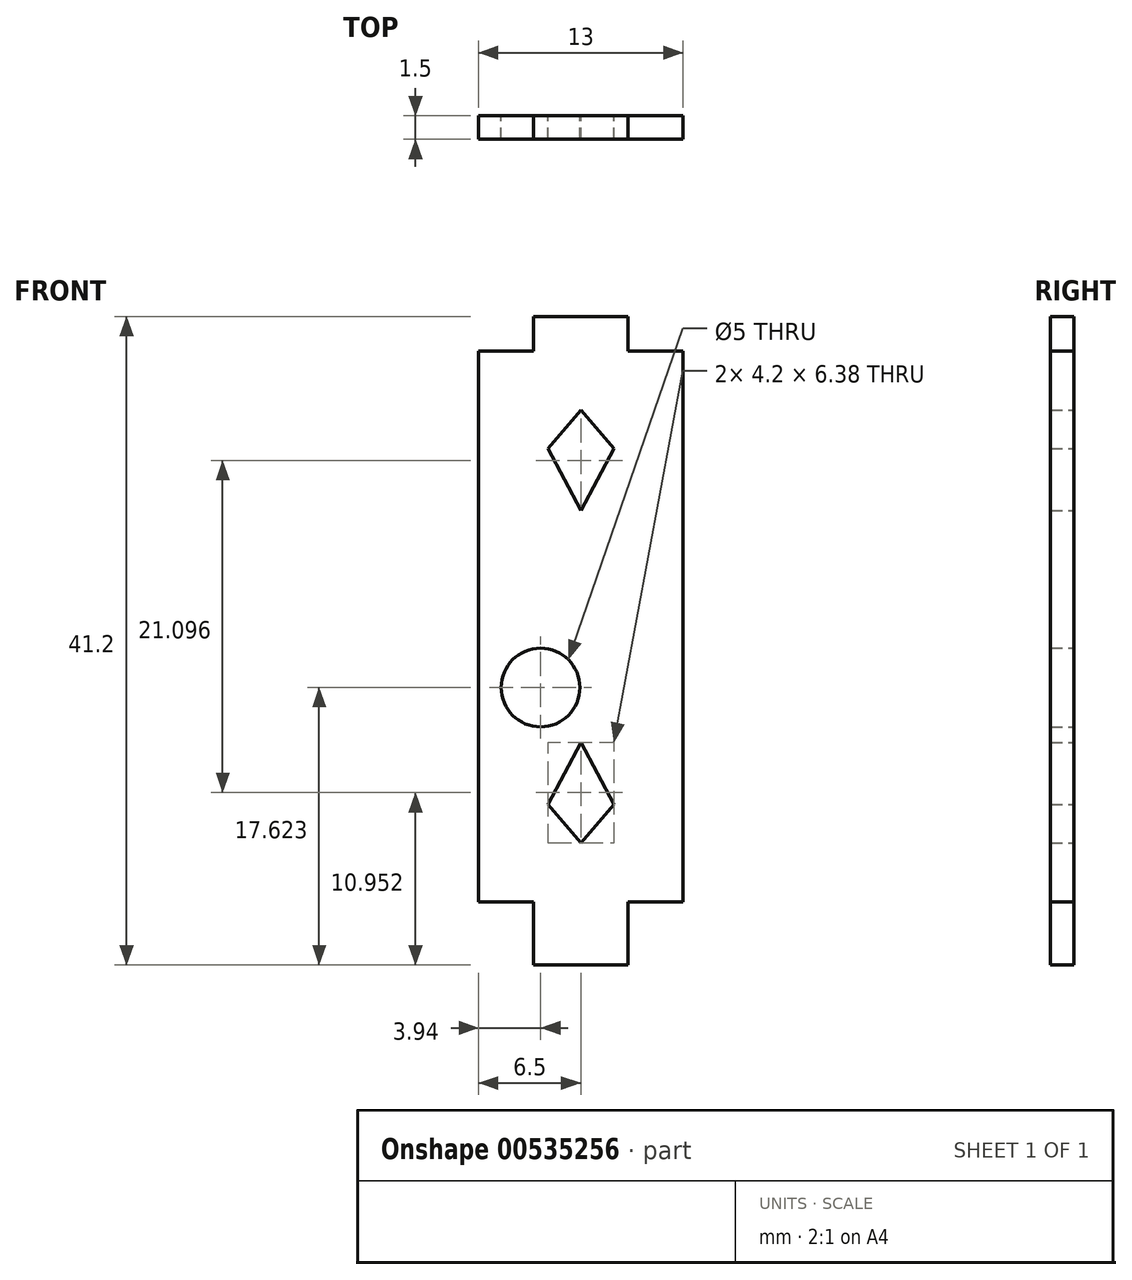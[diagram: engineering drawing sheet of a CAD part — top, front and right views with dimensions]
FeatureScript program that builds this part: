
annotation { "Feature Type Name" : "Feature", "Feature Type Description" : "" }
export const myFeature = defineFeature(function(context is Context, id is Id, definition is map)
    precondition{}
    {
        {
            var Q0;
            Q0=qCreatedBy(makeId("Front.planeOp"),FACE);
            var sketch = newSketch(context, id + "F0", { "sketchPlane" : qUnion([Q0])});
            skLineSegment(sketch, "E0.top", {"start": v(3, -2) * mm, "end": v(-3, -2) * mm});
            skLineSegment(sketch, "E0.left", {"start": v(3, 2) * mm, "end": v(3, -2) * mm});
            skLineSegment(sketch, "E0.right", {"start": v(-3, 2) * mm, "end": v(-3, -2) * mm});
            skPoint(sketch, "E0.middle", {"position": v(0, 0) * mm});
            skLineSegment(sketch, "E1", {"start": v(3, 2) * mm, "end": v(6.5, 2) * mm});
            skLineSegment(sketch, "E2", {"start": v(6.5, 2) * mm, "end": v(6.5, 37) * mm});
            skLineSegment(sketch, "E3", {"start": v(6.5, 37) * mm, "end": v(3, 37) * mm});
            skPoint(sketch, "E4", {"position": v(3, 37) * mm});
            skLineSegment(sketch, "E5.top", {"start": v(3, 39.2) * mm, "end": v(0, 39.2) * mm});
            skLineSegment(sketch, "E5.left", {"start": v(3, 37) * mm, "end": v(3, 39.2) * mm});
            skPoint(sketch, "E6.positionSnap0", {"position": v(6.5, 19.5) * mm});
            skLineSegment(sketch, "E7.MirrorCS", {"start": v(-3, 37) * mm, "end": v(-3, 39.2) * mm});
            skLineSegment(sketch, "E8.MirrorCS", {"start": v(-3, 39.2) * mm, "end": v(0, 39.2) * mm});
            skPoint(sketch, "E9.MirrorP", {"position": v(-3, 37) * mm});
            skLineSegment(sketch, "E10.MirrorCS", {"start": v(-3, -2) * mm, "end": v(3, -2) * mm});
            skLineSegment(sketch, "E11.MirrorCS", {"start": v(-3, 2) * mm, "end": v(-6.5, 2) * mm});
            skPoint(sketch, "E12.MirrorP", {"position": v(-6.5, 19.5) * mm});
            skLineSegment(sketch, "E13.MirrorCS", {"start": v(-6.5, 2) * mm, "end": v(-6.5, 37) * mm});
            skLineSegment(sketch, "E14.MirrorCS", {"start": v(-6.5, 37) * mm, "end": v(-3, 37) * mm});
            skPoint(sketch, "E15", {"position": v(-2.56, 19.5) * mm});
            skCircle(sketch, "E16", {"center": v(-2.56, 15.62) * mm, "radius": 2.5 * mm});
            skLineSegment(sketch, "E17", {"start": v(0, 33.24) * mm, "end": v(2.1, 30.8) * mm});
            skLineSegment(sketch, "E18", {"start": v(2.1, 30.8) * mm, "end": v(0, 26.86) * mm});
            skLineSegment(sketch, "E19.MirrorCS", {"start": v(-2.1, 30.8) * mm, "end": v(0, 26.86) * mm});
            skLineSegment(sketch, "E20.MirrorCS", {"start": v(0, 33.24) * mm, "end": v(-2.1, 30.8) * mm});
            skLineSegment(sketch, "E21.MirrorCS", {"start": v(0, 5.76) * mm, "end": v(-2.1, 8.2) * mm});
            skLineSegment(sketch, "E22.MirrorCS", {"start": v(0, 5.76) * mm, "end": v(2.1, 8.2) * mm});
            skLineSegment(sketch, "E23.MirrorCS", {"start": v(-2.1, 8.2) * mm, "end": v(0, 12.14) * mm});
            skLineSegment(sketch, "E24.MirrorCS", {"start": v(2.1, 8.2) * mm, "end": v(0, 12.14) * mm});
            skSolve(sketch);
        }
        {
            var Q0;
            Q0 = qSketchRegion(id + "F0", true);
            extrude(context, id + "F1", {"entities" : qUnion([Q0]), "depth" : 1.5 * mm, "offsetDistance" : 25 * mm});
        }
    });
